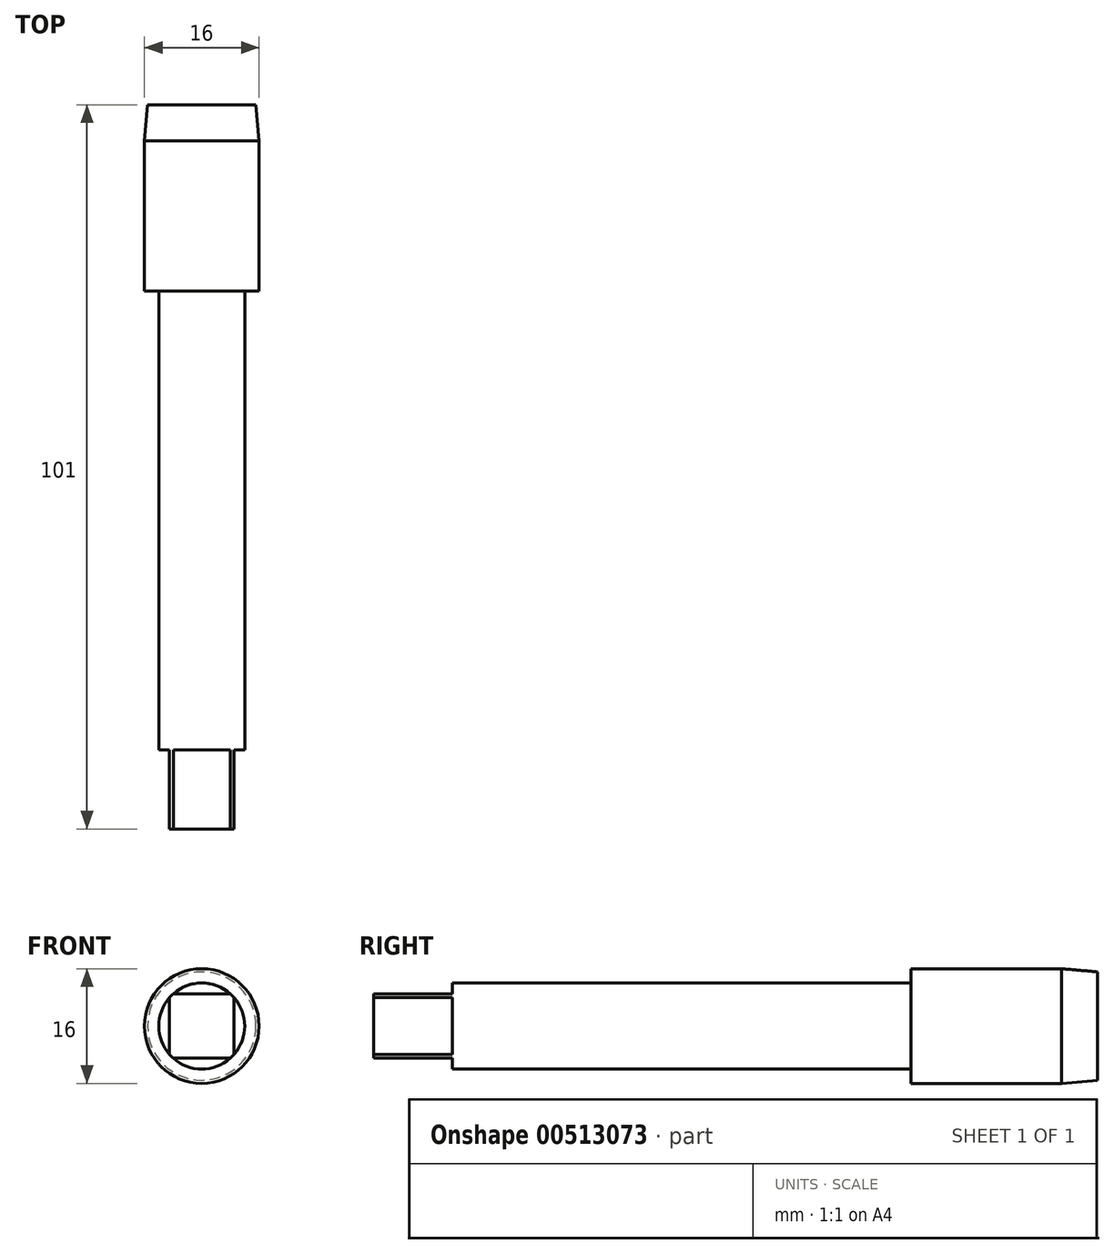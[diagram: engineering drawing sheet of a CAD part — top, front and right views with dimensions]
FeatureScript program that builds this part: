
annotation { "Feature Type Name" : "Feature", "Feature Type Description" : "" }
export const myFeature = defineFeature(function(context is Context, id is Id, definition is map)
    precondition{}
    {
        {
            var Q0;
            Q0=qCreatedBy(makeId("Front.planeOp"),FACE);
            var sketch = newSketch(context, id + "F0", { "sketchPlane" : qUnion([Q0])});
            skCircle(sketch, "E0", {"center": v(0, 0) * mm, "radius": 6 * mm});
            skSolve(sketch);
        }
        {
            var Q0;
            Q0 = qSketchRegion(id + "F0", true);
            extrude(context, id + "F1", {"entities" : qUnion([Q0]), "depth" : 75 * mm});
        }
        {
            var Q0;
            Q0=makeQuery(id+"F1.opExtrude","CAP_FACE",FACE,{"disambiguationData":[OSD([sQuery(id+"F0.wireOp",EDGE,"E0")])],"isStart":false});
            var sketch = newSketch(context, id + "F2", { "sketchPlane" : qUnion([Q0])});
            skLineSegment(sketch, "E1.bottom", {"start": v(-4.5, -4.5) * mm, "end": v(4.5, -4.5) * mm});
            skLineSegment(sketch, "E1.top", {"start": v(-4.5, 4.5) * mm, "end": v(4.5, 4.5) * mm});
            skLineSegment(sketch, "E1.left", {"start": v(-4.5, -4.5) * mm, "end": v(-4.5, 4.5) * mm});
            skLineSegment(sketch, "E1.right", {"start": v(4.5, -4.5) * mm, "end": v(4.5, 4.5) * mm});
            skPoint(sketch, "E1.middle", {"position": v(0, 0) * mm});
            skSolve(sketch);
        }
        {
            var Q0;
            {var subQ0=sQuery(id+"F2.wireOp",EDGE,"E1.right");var subQ1=makeQuery(id+"F1.opExtrude","CAP_EDGE",EDGE,{"disambiguationData":[OSD([sQuery(id+"F0.wireOp",EDGE,"E0")])],"isStart":false});var subQ2=makeQuery(id+"F2.imprint","INTERSECT",VERTEX,{"disambiguationData":[OD(0.0)],"derivedFrom":[subQ1,subQ0]});Q0=makeQuery(id+"F2.imprint","IMPRINT",FACE,{"disambiguationData":[TD([[makeQuery(id+"F2.imprint","IMPRINT",EDGE,{"disambiguationData":[TD([[subQ2,-1.0]])],"derivedFrom":subQ0}),-1.0]])]});}
            var Q1;
            {var subQ0=sQuery(id+"F2.wireOp",EDGE,"E1.top");var subQ1=makeQuery(id+"F1.opExtrude","CAP_EDGE",EDGE,{"disambiguationData":[OSD([sQuery(id+"F0.wireOp",EDGE,"E0")])],"isStart":false});var subQ2=makeQuery(id+"F2.imprint","INTERSECT",VERTEX,{"disambiguationData":[OD(0.0)],"derivedFrom":[subQ1,subQ0]});Q1=makeQuery(id+"F2.imprint","IMPRINT",FACE,{"disambiguationData":[TD([[makeQuery(id+"F2.imprint","IMPRINT",EDGE,{"disambiguationData":[TD([[subQ2,-1.0]])],"derivedFrom":subQ0}),1.0]])]});}
            var Q2;
            {var subQ0=sQuery(id+"F2.wireOp",EDGE,"E1.bottom");var subQ1=makeQuery(id+"F1.opExtrude","CAP_EDGE",EDGE,{"disambiguationData":[OSD([sQuery(id+"F0.wireOp",EDGE,"E0")])],"isStart":false});var subQ2=makeQuery(id+"F2.imprint","INTERSECT",VERTEX,{"disambiguationData":[OD(0.0)],"derivedFrom":[subQ1,subQ0]});Q2=makeQuery(id+"F2.imprint","IMPRINT",FACE,{"disambiguationData":[TD([[makeQuery(id+"F2.imprint","IMPRINT",EDGE,{"disambiguationData":[TD([[subQ2,-1.0]])],"derivedFrom":subQ0}),-1.0]])]});}
            var Q3;
            {var subQ0=sQuery(id+"F2.wireOp",EDGE,"E1.left");var subQ1=makeQuery(id+"F1.opExtrude","CAP_EDGE",EDGE,{"disambiguationData":[OSD([sQuery(id+"F0.wireOp",EDGE,"E0")])],"isStart":false});var subQ2=makeQuery(id+"F2.imprint","INTERSECT",VERTEX,{"disambiguationData":[OD(0.0)],"derivedFrom":[subQ1,subQ0]});Q3=makeQuery(id+"F2.imprint","IMPRINT",FACE,{"disambiguationData":[TD([[makeQuery(id+"F2.imprint","IMPRINT",EDGE,{"disambiguationData":[TD([[subQ2,-1.0]])],"derivedFrom":subQ0}),1.0]])]});}
            extrude(context, id + "F3", {"entities" : qUnion([Q0, Q1, Q2, Q3]), "operationType" : NewBodyOperationType.REMOVE, "oppositeDirection" : true, "depth" : 11 * mm});
        }
        {
            var Q0;
            Q0=makeQuery(id+"F1.opExtrude","CAP_FACE",FACE,{"disambiguationData":[OSD([sQuery(id+"F0.wireOp",EDGE,"E0")])],"isStart":true});
            var sketch = newSketch(context, id + "F4", { "sketchPlane" : qUnion([Q0])});
            skCircle(sketch, "E2", {"center": v(0, 0) * mm, "radius": 8 * mm});
            skSolve(sketch);
        }
        {
            var Q0;
            Q0 = qSketchRegion(id + "F4", true);
            extrude(context, id + "F5", {"entities" : qUnion([Q0]), "operationType" : NewBodyOperationType.ADD, "depth" : 26 * mm});
        }
        {
            var Q0;
            Q0=makeQuery(id+"F5.opExtrude","CAP_EDGE",EDGE,{"disambiguationData":[OSD([sQuery(id+"F4.wireOp",EDGE,"E2")])],"isStart":false});
            chamfer(context, id + "F6", {"entities" : qUnion([Q0]), "chamferType" : ChamferType.OFFSET_ANGLE, "width" : 5 * mm, "oppositeDirection" : true, "angle" : 5 * degree, "tangentPropagation" : true});
        }
    });
